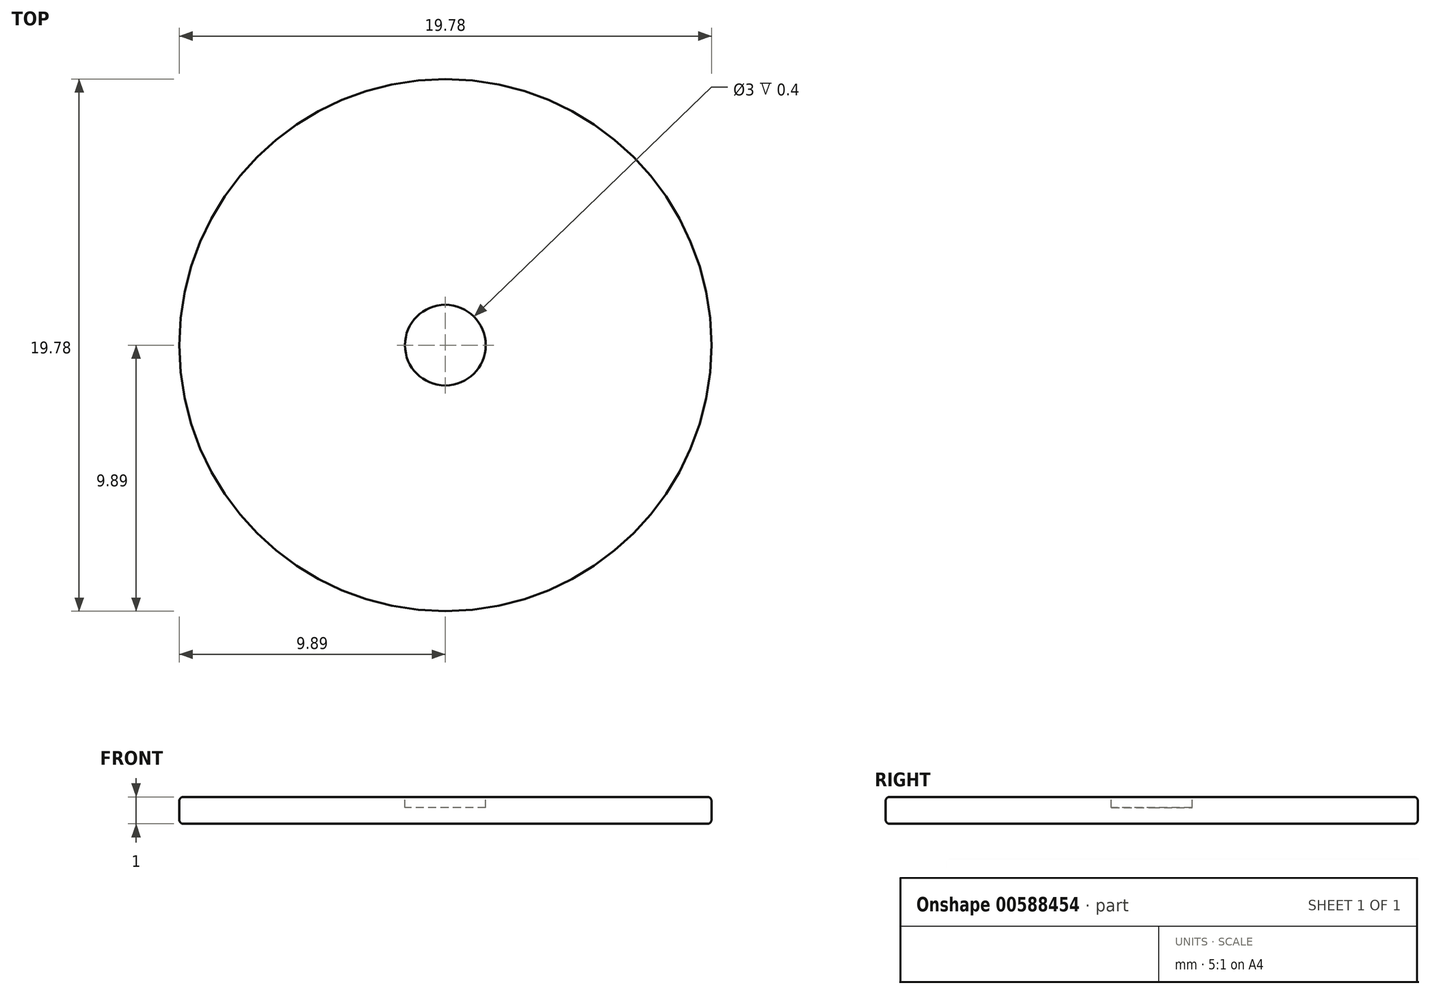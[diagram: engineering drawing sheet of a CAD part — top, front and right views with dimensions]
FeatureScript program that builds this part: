
annotation { "Feature Type Name" : "Feature", "Feature Type Description" : "" }
export const myFeature = defineFeature(function(context is Context, id is Id, definition is map)
    precondition{}
    {
        {
            var Q0;
            Q0=qCreatedBy(makeId("Top.planeOp"),FACE);
            var sketch = newSketch(context, id + "F0", { "sketchPlane" : qUnion([Q0])});
            skCircle(sketch, "E0", {"center": v(0, 0) * mm, "radius": 9.88 * mm});
            skSolve(sketch);
        }
        {
            var Q0;
            Q0 = qSketchRegion(id + "F0", true);
            var Q1;
            Q1 = qSketchRegion(id + "F3", true);
            extrude(context, id + "F1", {"entities" : qUnion([Q0, Q1]), "depth" : 1 * mm, "offsetDistance" : 25 * mm});
        }
        {
            var Q0;
            Q0=makeQuery(id+"F1.opExtrude","CAP_EDGE",EDGE,{"disambiguationData":[OSD([sQuery(id+"F0.wireOp",EDGE,"E0")])],"isStart":false});
            var Q1;
            Q1=makeQuery(id+"F1.opExtrude","CAP_EDGE",EDGE,{"disambiguationData":[OSD([sQuery(id+"F0.wireOp",EDGE,"E0")])],"isStart":true});
            fillet(context, id + "F2", {"entities" : qUnion([Q0, Q1]), "radius" : 0.15 * mm, "tangentPropagation" : true, "allowEdgeOverflow" : false});
        }
        {
            var Q0;
            Q0=makeQuery(id+"F1.opExtrude","CAP_FACE",FACE,{"disambiguationData":[OSD([sQuery(id+"F0.wireOp",EDGE,"E0")])],"isStart":false});
            var sketch = newSketch(context, id + "F3", { "sketchPlane" : qUnion([Q0])});
            skCircle(sketch, "E1", {"center": v(0, 0) * mm, "radius": 1.5 * mm});
            skSolve(sketch);
        }
        {
            var Q0;
            Q0 = qSketchRegion(id + "F3", true);
            extrude(context, id + "F4", {"entities" : qUnion([Q0]), "operationType" : NewBodyOperationType.REMOVE, "oppositeDirection" : true, "depth" : 0.4 * mm, "offsetDistance" : 25 * mm});
        }
    });
